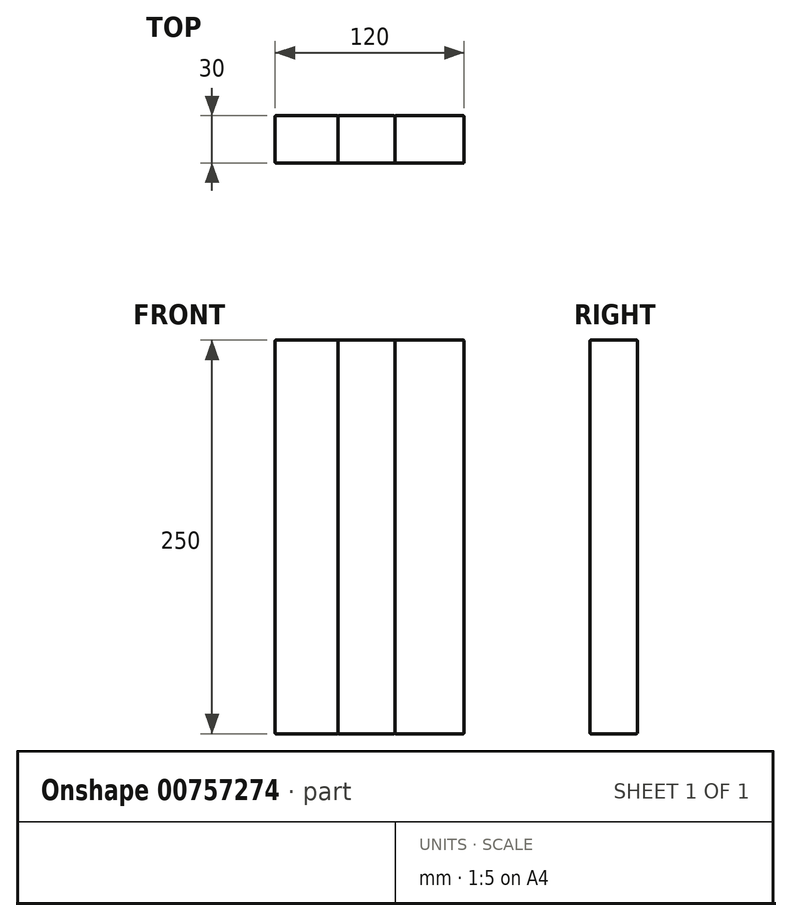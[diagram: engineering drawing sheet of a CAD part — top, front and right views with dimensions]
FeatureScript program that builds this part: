
annotation { "Feature Type Name" : "Feature", "Feature Type Description" : "" }
export const myFeature = defineFeature(function(context is Context, id is Id, definition is map)
    precondition{}
    {
        {
            var Q0;
            Q0=qCreatedBy(makeId("Front.planeOp"),FACE);
            var sketch = newSketch(context, id + "F0", { "sketchPlane" : qUnion([Q0])});
            skLineSegment(sketch, "E0.bottom", {"start": v(-40, 0) * mm, "end": v(0, 0) * mm});
            skLineSegment(sketch, "E0.top", {"start": v(-40, 250) * mm, "end": v(0, 250) * mm});
            skLineSegment(sketch, "E0.left", {"start": v(-40, 0) * mm, "end": v(-40, 250) * mm});
            skLineSegment(sketch, "E0.right", {"start": v(0, 0) * mm, "end": v(0, 250) * mm});
            skSolve(sketch);
        }
        {
            var Q0;
            Q0=qCreatedBy(makeId("Front.planeOp"),FACE);
            var sketch = newSketch(context, id + "F1", { "sketchPlane" : qUnion([Q0])});
            skLineSegment(sketch, "E1.bottom", {"start": v(0, 0) * mm, "end": v(36, 0) * mm});
            skLineSegment(sketch, "E1.top", {"start": v(0, 250) * mm, "end": v(36, 250) * mm});
            skLineSegment(sketch, "E1.left", {"start": v(0, 0) * mm, "end": v(0, 250) * mm});
            skLineSegment(sketch, "E1.right", {"start": v(36, 0) * mm, "end": v(36, 250) * mm});
            skSolve(sketch);
        }
        {
            var Q0;
            Q0=qCreatedBy(makeId("Front.planeOp"),FACE);
            var sketch = newSketch(context, id + "F2", { "sketchPlane" : qUnion([Q0])});
            skLineSegment(sketch, "E2.bottom", {"start": v(36, 0) * mm, "end": v(80, 0) * mm});
            skLineSegment(sketch, "E2.top", {"start": v(36, 250) * mm, "end": v(80, 250) * mm});
            skLineSegment(sketch, "E2.left", {"start": v(36, 0) * mm, "end": v(36, 250) * mm});
            skLineSegment(sketch, "E2.right", {"start": v(80, 0) * mm, "end": v(80, 250) * mm});
            skSolve(sketch);
        }
        {
            var Q0;
            Q0 = qSketchRegion(id + "F0", true);
            extrude(context, id + "F3", {"entities" : qUnion([Q0]), "depth" : 30 * mm, "offsetDistance" : 25 * mm});
        }
        {
            var Q0;
            Q0=makeQuery(id+"F1.imprint","IMPRINT",FACE,{"disambiguationData":[TD([[makeQuery(id+"F1.imprint","IMPRINT",EDGE,{"derivedFrom":sQuery(id+"F1.wireOp",EDGE,"E1.bottom")}),1.0]])]});
            extrude(context, id + "F4", {"entities" : qUnion([Q0]), "depth" : 30 * mm, "offsetDistance" : 25 * mm});
        }
        {
            var Q0;
            Q0=makeQuery(id+"F2.imprint","IMPRINT",FACE,{"disambiguationData":[TD([[makeQuery(id+"F2.imprint","IMPRINT",EDGE,{"derivedFrom":sQuery(id+"F2.wireOp",EDGE,"E2.bottom")}),1.0]])]});
            extrude(context, id + "F5", {"entities" : qUnion([Q0]), "depth" : 30 * mm, "offsetDistance" : 25 * mm});
        }
        {
            var Q0;
            Q0=makeQuery(id+"F5.opExtrude","CAP_EDGE",EDGE,{"disambiguationData":[OSD([sQuery(id+"F2.wireOp",EDGE,"E2.right")])],"isStart":false});
            var Q1;
            Q1=makeQuery(id+"F5.opExtrude","CAP_FACE",FACE,{"disambiguationData":[OSD([sQuery(id+"F2.wireOp",EDGE,"E2.bottom"),sQuery(id+"F2.wireOp",EDGE,"E2.top"),sQuery(id+"F2.wireOp",EDGE,"E2.left"),sQuery(id+"F2.wireOp",EDGE,"E2.right")])],"isStart":false});
            var Q2;
            Q2=makeQuery(id+"F4.opExtrude","CAP_FACE",FACE,{"disambiguationData":[OSD([sQuery(id+"F1.wireOp",EDGE,"E1.bottom"),sQuery(id+"F1.wireOp",EDGE,"E1.top"),sQuery(id+"F1.wireOp",EDGE,"E1.left"),sQuery(id+"F1.wireOp",EDGE,"E1.right")])],"isStart":false});
            var Q3;
            Q3=makeQuery(id+"F3.opExtrude","CAP_FACE",FACE,{"disambiguationData":[OSD([sQuery(id+"F0.wireOp",EDGE,"E0.bottom"),sQuery(id+"F0.wireOp",EDGE,"E0.top"),sQuery(id+"F0.wireOp",EDGE,"E0.left"),sQuery(id+"F0.wireOp",EDGE,"E0.right")])],"isStart":false});
            var Q4;
            Q4=makeQuery(id+"F3.opExtrude","SWEPT_FACE",FACE,{"disambiguationData":[OSD([sQuery(id+"F0.wireOp",EDGE,"E0.top")])]});
            var Q5;
            Q5=makeQuery(id+"F5.opExtrude","CAP_EDGE",EDGE,{"disambiguationData":[OSD([sQuery(id+"F2.wireOp",EDGE,"E2.top")])],"isStart":false});
            var Q6;
            Q6=makeQuery(id+"F3.opExtrude","SWEPT_EDGE",EDGE,{"disambiguationData":[OSD([sQuery(id+"F0.wireOp",EDGE,"E0.top"),sQuery(id+"F0.wireOp",EDGE,"E0.right")])]});
            var Q7;
            Q7=makeQuery(id+"F5.opExtrude","CAP_FACE",FACE,{"disambiguationData":[OSD([sQuery(id+"F2.wireOp",EDGE,"E2.bottom"),sQuery(id+"F2.wireOp",EDGE,"E2.top"),sQuery(id+"F2.wireOp",EDGE,"E2.left"),sQuery(id+"F2.wireOp",EDGE,"E2.right")])],"isStart":true});
            var Q8;
            Q8=makeQuery(id+"F4.opExtrude","CAP_FACE",FACE,{"disambiguationData":[OSD([sQuery(id+"F1.wireOp",EDGE,"E1.bottom"),sQuery(id+"F1.wireOp",EDGE,"E1.top"),sQuery(id+"F1.wireOp",EDGE,"E1.left"),sQuery(id+"F1.wireOp",EDGE,"E1.right")])],"isStart":true});
            var Q9;
            Q9=makeQuery(id+"F3.opExtrude","CAP_FACE",FACE,{"disambiguationData":[OSD([sQuery(id+"F0.wireOp",EDGE,"E0.bottom"),sQuery(id+"F0.wireOp",EDGE,"E0.top"),sQuery(id+"F0.wireOp",EDGE,"E0.left"),sQuery(id+"F0.wireOp",EDGE,"E0.right")])],"isStart":true});
            var Q10;
            Q10=makeQuery(id+"F3.opExtrude","SWEPT_FACE",FACE,{"disambiguationData":[OSD([sQuery(id+"F0.wireOp",EDGE,"E0.left")])]});
            var Q11;
            Q11=makeQuery(id+"F5.opExtrude","SWEPT_FACE",FACE,{"disambiguationData":[OSD([sQuery(id+"F2.wireOp",EDGE,"E2.right")])]});
            var Q12;
            Q12=makeQuery(id+"F5.opExtrude","SWEPT_FACE",FACE,{"disambiguationData":[OSD([sQuery(id+"F2.wireOp",EDGE,"E2.bottom")])]});
            var Q13;
            Q13=makeQuery(id+"F4.opExtrude","SWEPT_FACE",FACE,{"disambiguationData":[OSD([sQuery(id+"F1.wireOp",EDGE,"E1.bottom")])]});
            var Q14;
            Q14=makeQuery(id+"F3.opExtrude","SWEPT_FACE",FACE,{"disambiguationData":[OSD([sQuery(id+"F0.wireOp",EDGE,"E0.bottom")])]});
            fillet(context, id + "F6", {"entities" : qUnion([Q0, Q1, Q2, Q3, Q4, Q5, Q6, Q7, Q8, Q9, Q10, Q11, Q12, Q13, Q14]), "radius" : 0.5 * mm, "tangentPropagation" : true, "allowEdgeOverflow" : false});
        }
    });
